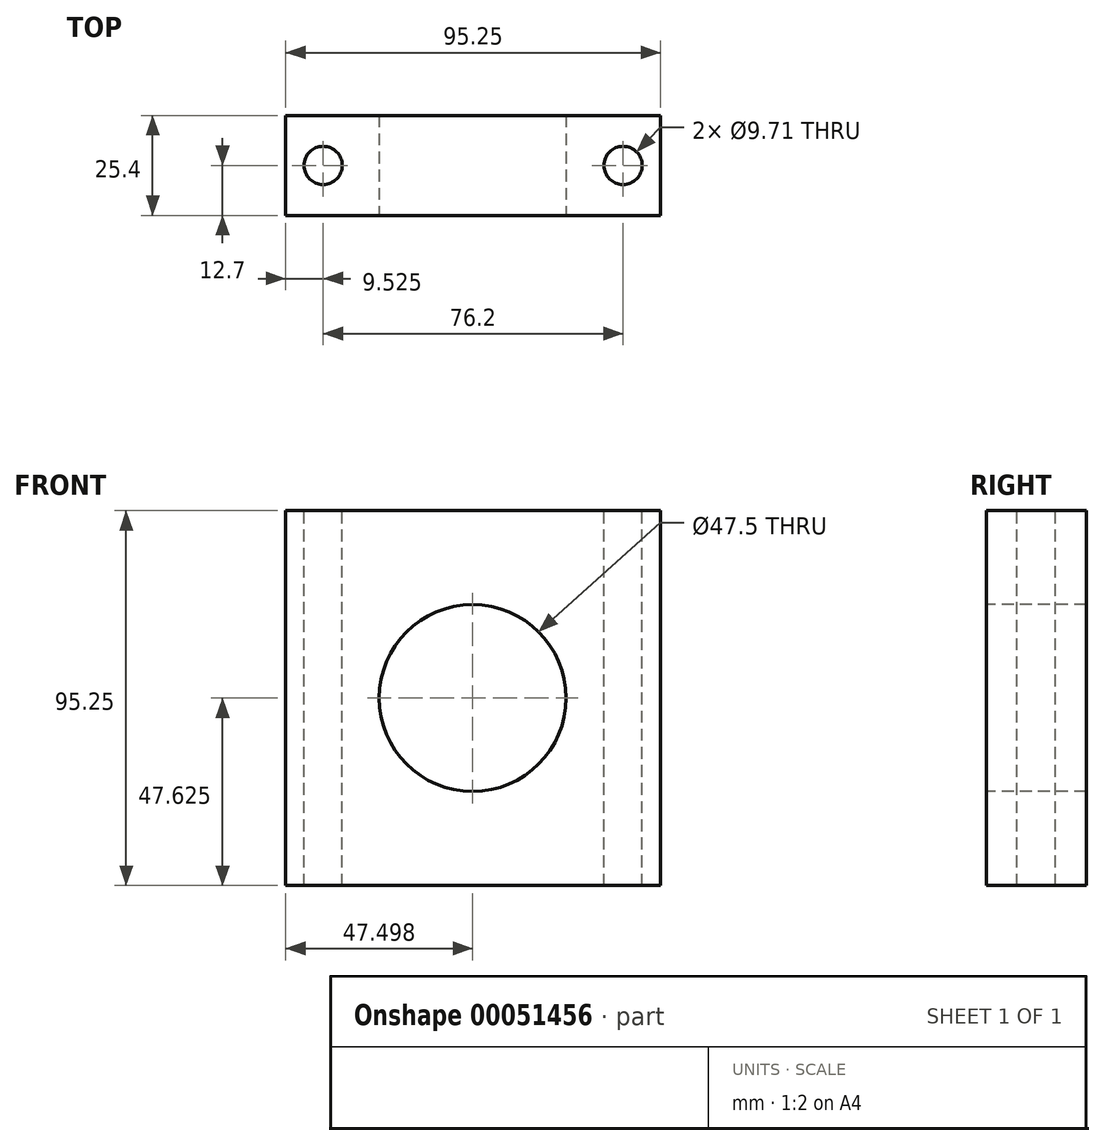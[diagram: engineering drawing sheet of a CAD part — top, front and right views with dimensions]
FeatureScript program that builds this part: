
annotation { "Feature Type Name" : "Feature", "Feature Type Description" : "" }
export const myFeature = defineFeature(function(context is Context, id is Id, definition is map)
    precondition{}
    {
        {
            var Q0;
            Q0=qCreatedBy(makeId("Front.planeOp"),FACE);
            var sketch = newSketch(context, id + "F0", { "sketchPlane" : qUnion([Q0])});
            skLineSegment(sketch, "E0.bottom", {"start": v(0, 0) * mm, "end": v(-95.25, 0) * mm});
            skLineSegment(sketch, "E0.top", {"start": v(0, 95.25) * mm, "end": v(-95.25, 95.25) * mm});
            skLineSegment(sketch, "E0.left", {"start": v(0, 0) * mm, "end": v(0, 95.25) * mm});
            skLineSegment(sketch, "E0.right", {"start": v(-95.25, 0) * mm, "end": v(-95.25, 95.25) * mm});
            skSolve(sketch);
        }
        {
            var Q0;
            Q0 = qSketchRegion(id + "F0", true);
            extrude(context, id + "F1", {"entities" : qUnion([Q0]), "depth" : 25.4 * mm});
        }
        {
            var Q0;
            Q0=makeQuery(id+"F1.opExtrude","CAP_FACE",FACE,{"disambiguationData":[OSD([sQuery(id+"F0.wireOp",EDGE,"E0.bottom"),sQuery(id+"F0.wireOp",EDGE,"E0.top"),sQuery(id+"F0.wireOp",EDGE,"E0.left"),sQuery(id+"F0.wireOp",EDGE,"E0.right")])],"isStart":false});
            var sketch = newSketch(context, id + "F2", { "sketchPlane" : qUnion([Q0])});
            skLineSegment(sketch, "E1.0", {"start": v(-47.75, 0) * mm, "end": v(-47.75, 95.25) * mm, "construction": true});
            skCircle(sketch, "E2", {"center": v(-47.75, 47.63) * mm, "radius": 23.75 * mm});
            skSolve(sketch);
        }
        {
            var Q0;
            Q0 = qSketchRegion(id + "F2", true);
            extrude(context, id + "F3", {"entities" : qUnion([Q0]), "operationType" : NewBodyOperationType.REMOVE, "endBound" : BoundingType.THROUGH_ALL, "oppositeDirection" : true, "depth" : 25.4 * mm});
        }
        {
            var Q0;
            Q0=makeQuery(id+"F1.opExtrude","SWEPT_FACE",FACE,{"disambiguationData":[OSD([sQuery(id+"F0.wireOp",EDGE,"E0.top")])]});
            var sketch = newSketch(context, id + "F4", { "sketchPlane" : qUnion([Q0])});
            skLineSegment(sketch, "E3.0", {"start": v(-9.53, -25.4) * mm, "end": v(-9.53, 0) * mm, "construction": true});
            skLineSegment(sketch, "E4.0", {"start": v(6.35, 6.35) * mm, "end": v(-101.6, 6.35) * mm, "construction": true});
            skLineSegment(sketch, "E4.1", {"start": v(6.35, -31.75) * mm, "end": v(6.35, 6.35) * mm, "construction": true});
            skLineSegment(sketch, "E4.2", {"start": v(-101.6, -31.75) * mm, "end": v(6.35, -31.75) * mm, "construction": true});
            skLineSegment(sketch, "E4.3", {"start": v(-101.6, 6.35) * mm, "end": v(-101.6, -31.75) * mm, "construction": true});
            skLineSegment(sketch, "E5", {"start": v(-47.63, 0) * mm, "end": v(-47.63, -25.4) * mm, "construction": true});
            skCircle(sketch, "E6", {"center": v(-9.53, -12.7) * mm, "radius": 4.86 * mm});
            skCircle(sketch, "E7.MirrorC", {"center": v(-85.73, -12.7) * mm, "radius": 4.86 * mm});
            skSolve(sketch);
        }
        {
            var Q0;
            Q0 = qSketchRegion(id + "F4", true);
            extrude(context, id + "F5", {"entities" : qUnion([Q0]), "operationType" : NewBodyOperationType.REMOVE, "endBound" : BoundingType.THROUGH_ALL, "oppositeDirection" : true, "depth" : 25.4 * mm});
        }
    });
